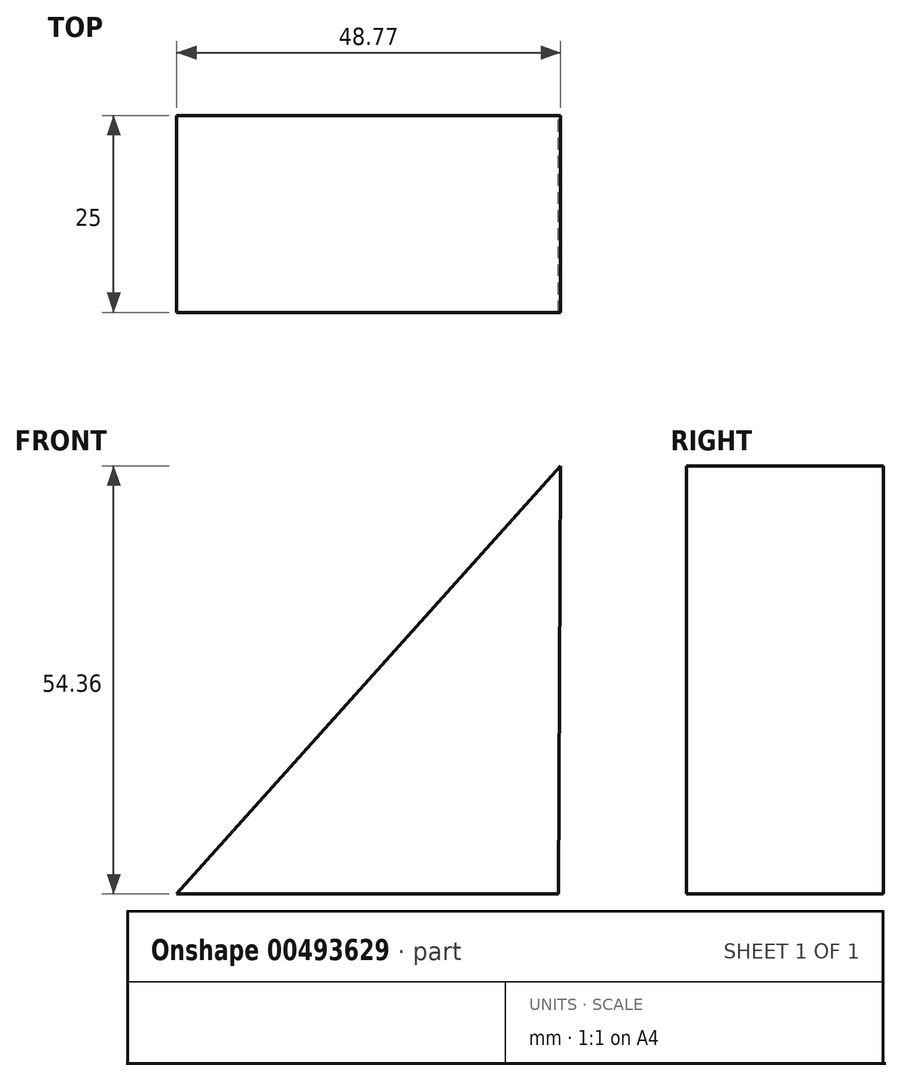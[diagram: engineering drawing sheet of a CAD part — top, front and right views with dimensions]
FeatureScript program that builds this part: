
annotation { "Feature Type Name" : "Feature", "Feature Type Description" : "" }
export const myFeature = defineFeature(function(context is Context, id is Id, definition is map)
    precondition{}
    {
        {
            var Q0;
            Q0=qCreatedBy(makeId("Front.planeOp"),FACE);
            var sketch = newSketch(context, id + "F0", { "sketchPlane" : qUnion([Q0])});
            skLineSegment(sketch, "E0", {"start": v(0, 0) * mm, "end": v(-48.77, 0) * mm});
            skLineSegment(sketch, "E1", {"start": v(-48.77, 0) * mm, "end": v(0, 54.36) * mm});
            skLineSegment(sketch, "E2", {"start": v(0, 54.36) * mm, "end": v(-0.29, -0.14) * mm});
            skSolve(sketch);
        }
        {
            var Q0;
            {var subQ0=sQuery(id+"F0.wireOp",EDGE,"E1");Q0=makeQuery(id+"F0.imprint","IMPRINT",FACE,{"disambiguationData":[TD([[makeQuery(id+"F0.imprint","IMPRINT",EDGE,{"derivedFrom":subQ0}),-1.0]])]});}
            extrude(context, id + "F1", {"entities" : qUnion([Q0]), "depth" : 25 * mm});
        }
    });
